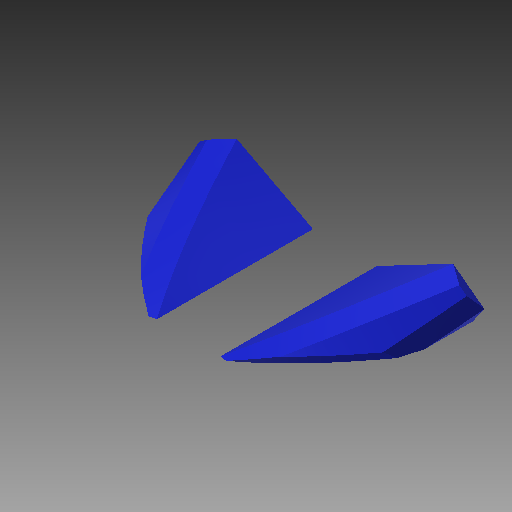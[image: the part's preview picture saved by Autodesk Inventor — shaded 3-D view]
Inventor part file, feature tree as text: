
AUTODESK INVENTOR PART (.ipt)
format: ipt  version: 2017 (Build 210142000, 142)  size: 227,840 bytes
history: native  units: in
note: dims shown in document units (in); Inventor stores cm internally (conversion verified against a paired STEP export)
features: sketch x3, plane x1, loft x1, extrude x1, chamfer x1
ambient origin geometry x8: Origin, YZ Plane, XZ Plane, XY Plane, X Axis, Y Axis, Z Axis, Center Point
bodies: Solid1 (feature_tree)
feature tree (7):
  sketch  "Sketch1"  dims[d0=0.7559in d1=0.7559in]
  plane  "Work Plane1"
  loft  "Main Body"
  extrude  "Create Eyes"  Depth=0.2in
  chamfer  "Eyes Chamfer"  Distance=0.08in
  sketch  "Sketch2"  dims[d2=0.9963in d3=0.2in]
  sketch  "Sketch3"  dims[d4=0.5in d6=0.08in d7=0.55in d8=150.0deg d9=150.0deg d14=0.33in d15=0.66in d18=0.0in d19=90.0deg d20=0.0in d21=90.0deg d22=1.0in d26=1.0651in d28=1.0651in d29=0.0in d30=0.962in d31=0.962in d32=0.075in d33=0.15in d34=0.06in d35=0.1in d36=0.05in d37=0.45in d38=0.0in d125=0.02in d126=0.125in d127=45.0deg]
